# Revit family: TAG3
name_source: partatom
category: Furniture
units: mm (PartAtom-declared; Revit-internal decimal feet)

## family parameters
Always vertical = Yes
Cut with Voids When Loaded = No
OmniClass Number = 23.40.20.00
OmniClass Title = General Furniture and Specialties
Render Appearance Source = Family Geometry
Room Calculation Point = No
Shared = No
Work Plane-Based = No

## types (1)
- CBCGTYP003
    Cost = 12039 $
    Default Elevation = 0 mm  [stored 0 ft]
    Description = 1 x Plastic Pencil Drawer 21 1/4W x 16 1/4D x 2 1/4H - Black, 1 x Silver Key Alike Kit (3 Cores) - Wesko Type, 1 x Cbx Partial Depth Bbf Ped 29dx28hx16w, 1 x Cb Desk Bridge With Full Mod Flush 20dx42wx29h, 1 x Cb Desk Shell Half Mod Recessed 24dx72wx29h, 1 x Cb Desk Shell With Full Mod Flush 30dx72wx29h, 1 x Cbx Full Depth Ff Ped 18dx28hx16w, 1 x Cbx Single Hutch With Cabinet Doors 14dx45hx72w, 1 x Cbx Tackboard Hutch Mount 28hx72w
    Exported From CET Designer = Yes
    Manufacturer = AIS
    Model = A-PDRWP
    Show CBCGTYP003 = Yes
    VisibilityIndex = 0

note: [stored X ft] marks values corroborated as IEEE doubles in the binary element streams (Revit-internal decimal feet)

## geometry (parser evidence)
native form markers: Sweep x3
no freeform markers — native parametric forms only
